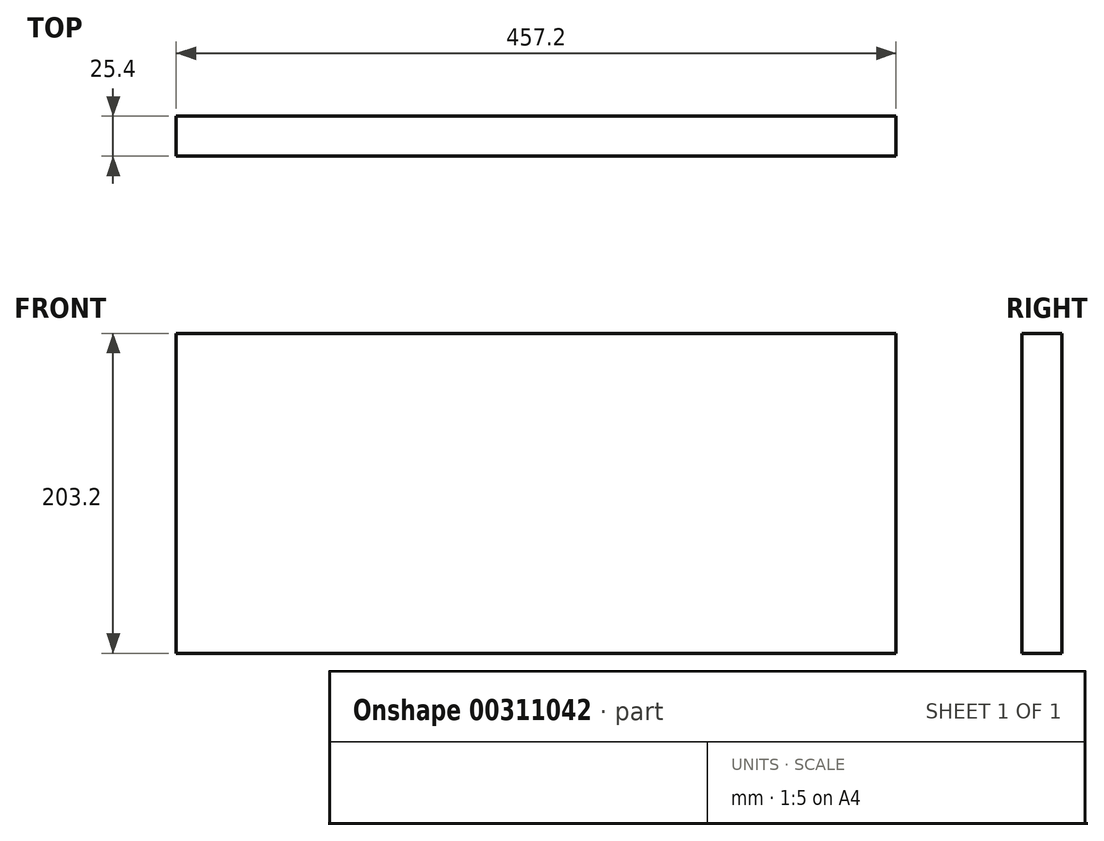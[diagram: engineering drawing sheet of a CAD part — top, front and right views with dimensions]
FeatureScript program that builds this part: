
annotation { "Feature Type Name" : "Feature", "Feature Type Description" : "" }
export const myFeature = defineFeature(function(context is Context, id is Id, definition is map)
    precondition{}
    {
        {
            var Q0;
            Q0=qCreatedBy(makeId("Front.planeOp"),FACE);
            var sketch = newSketch(context, id + "F0", { "sketchPlane" : qUnion([Q0])});
            skLineSegment(sketch, "E0.bottom", {"start": v(-457.2, 232.4) * mm, "end": v(0, 232.4) * mm});
            skLineSegment(sketch, "E0.top", {"start": v(-457.2, 29.2) * mm, "end": v(0, 29.2) * mm});
            skLineSegment(sketch, "E0.left", {"start": v(-457.2, 232.4) * mm, "end": v(-457.2, 29.2) * mm});
            skLineSegment(sketch, "E0.right", {"start": v(0, 232.4) * mm, "end": v(0, 29.2) * mm});
            skLineSegment(sketch, "E1", {"start": v(-228.6, 232.4) * mm, "end": v(-228.6, 29.2) * mm, "construction": true});
            skSolve(sketch);
        }
        {
            var Q0;
            Q0=makeQuery(id+"F0.imprint","IMPRINT",FACE,{"disambiguationData":[TD([[makeQuery(id+"F0.imprint","IMPRINT",EDGE,{"derivedFrom":sQuery(id+"F0.wireOp",EDGE,"E0.bottom")}),-1.0]])]});
            extrude(context, id + "F1", {"entities" : qUnion([Q0]), "depth" : 25.4 * mm});
        }
    });
